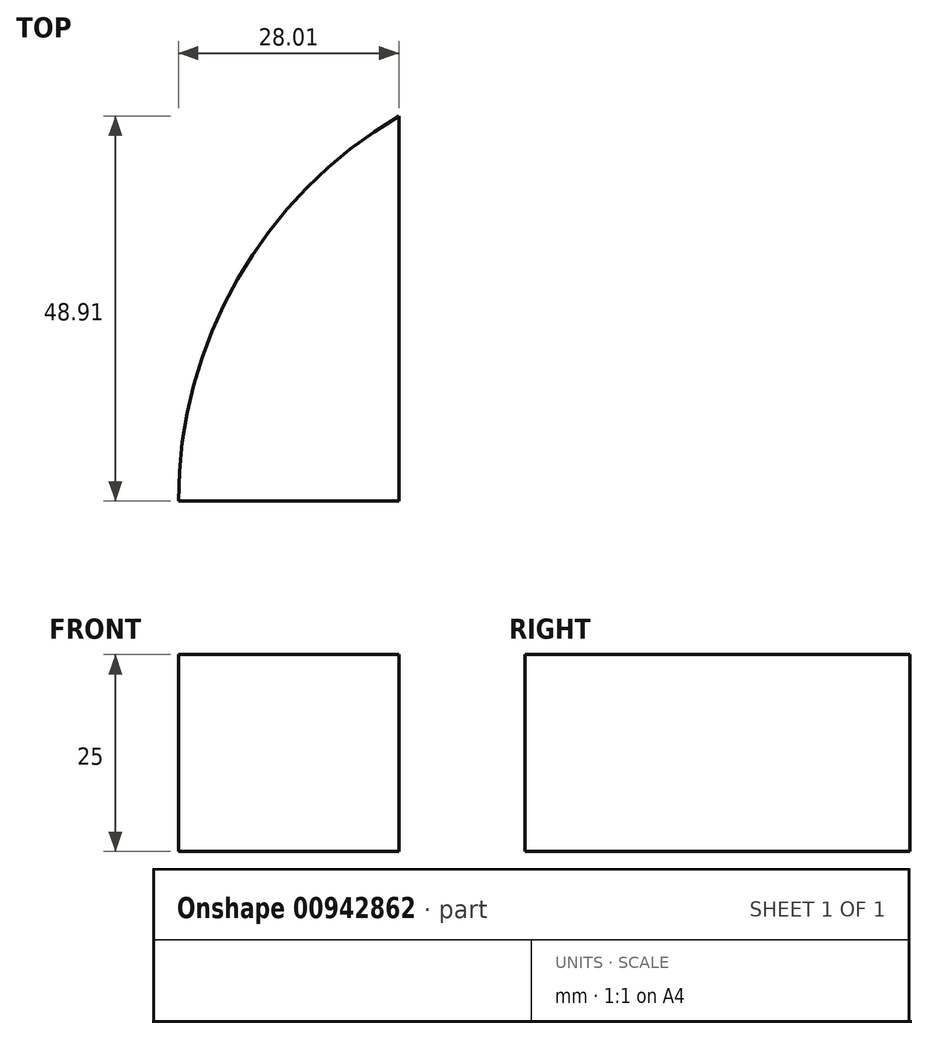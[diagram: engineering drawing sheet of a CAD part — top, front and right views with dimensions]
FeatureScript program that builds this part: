
annotation { "Feature Type Name" : "Feature", "Feature Type Description" : "" }
export const myFeature = defineFeature(function(context is Context, id is Id, definition is map)
    precondition{}
    {
        {
            var Q0;
            Q0=qCreatedBy(makeId("Top.planeOp"),FACE);
            var sketch = newSketch(context, id + "F0", { "sketchPlane" : qUnion([Q0])});
            skLineSegment(sketch, "E0.bottom", {"start": v(-68.21, 0) * mm, "end": v(5.24, 0) * mm});
            skLineSegment(sketch, "E0.top", {"start": v(-68.21, 48.9) * mm, "end": v(5.24, 48.9) * mm});
            skLineSegment(sketch, "E0.left", {"start": v(-68.21, 0) * mm, "end": v(-68.21, 48.9) * mm});
            skLineSegment(sketch, "E0.right", {"start": v(5.24, 0) * mm, "end": v(5.24, 48.9) * mm});
            skSolve(sketch);
        }
        {
            var Q0;
            Q0=qSketchRegion(id+"F0",true);
            extrude(context, id + "F1", {"entities" : qUnion([Q0]), "depth" : 25 * mm});
        }
        {
            var Q0;
            Q0=makeQuery(id+"F1.opExtrude","SWEPT_FACE",FACE,{"disambiguationData":[OSD([sQuery(id+"F0.wireOp",EDGE,"E0.bottom")])]});
            var sketch = newSketch(context, id + "F2", { "sketchPlane" : qUnion([Q0])});
            skLineSegment(sketch, "E1", {"start": v(33.94, 31.82) * mm, "end": v(33.94, -9.54) * mm});
            skSolve(sketch);
        }
        {
            var Q0;
            Q0=makeQuery(id+"F1.opExtrude","SWEPT_FACE",FACE,{"disambiguationData":[OSD([sQuery(id+"F0.wireOp",EDGE,"E0.right")])]});
            var Q1;
            Q1=sQuery(id+"F2.wireOp",EDGE,"E1");
            revolve(context, id + "F3", {"operationType" : NewBodyOperationType.INTERSECT, "entities" : qUnion([Q0]), "axis" : qUnion([Q1]), "revolveType" : RevolveType.FULL});
        }
    });
